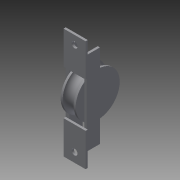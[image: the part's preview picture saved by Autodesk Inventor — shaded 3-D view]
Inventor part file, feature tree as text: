
AUTODESK INVENTOR PART (.ipt)
format: ipt  version: 2013 (Build 170138000, 138)  size: 163,328 bytes
history: native  units: mm
features: sketch x5, extrude x3, other x1, revolve x1, hole x1
ambient origin geometry x8: Origin, YZ Plane, XZ Plane, XY Plane, X Axis, Y Axis, Z Axis, Center Point
feature tree (11):
  other  "ソリッド1"
  revolve  "回転1"
  extrude  "押し出し1"  Depth=8.2mm
  extrude  "押し出し2"  Depth=12.0mm
  extrude  "押し出し3"  Depth=12.0mm
  hole  "穴1"  [1 undecoded]
  sketch  "スケッチ1"
  sketch  "スケッチ2"
  sketch  "スケッチ3"
  sketch  "スケッチ4"
  sketch  "スケッチ5"
note: 1 required parameter value undecoded (feature->parameter linkage not recoverable at this tier; creation-order binding heuristic only, values carry confidence <= 0.55)
